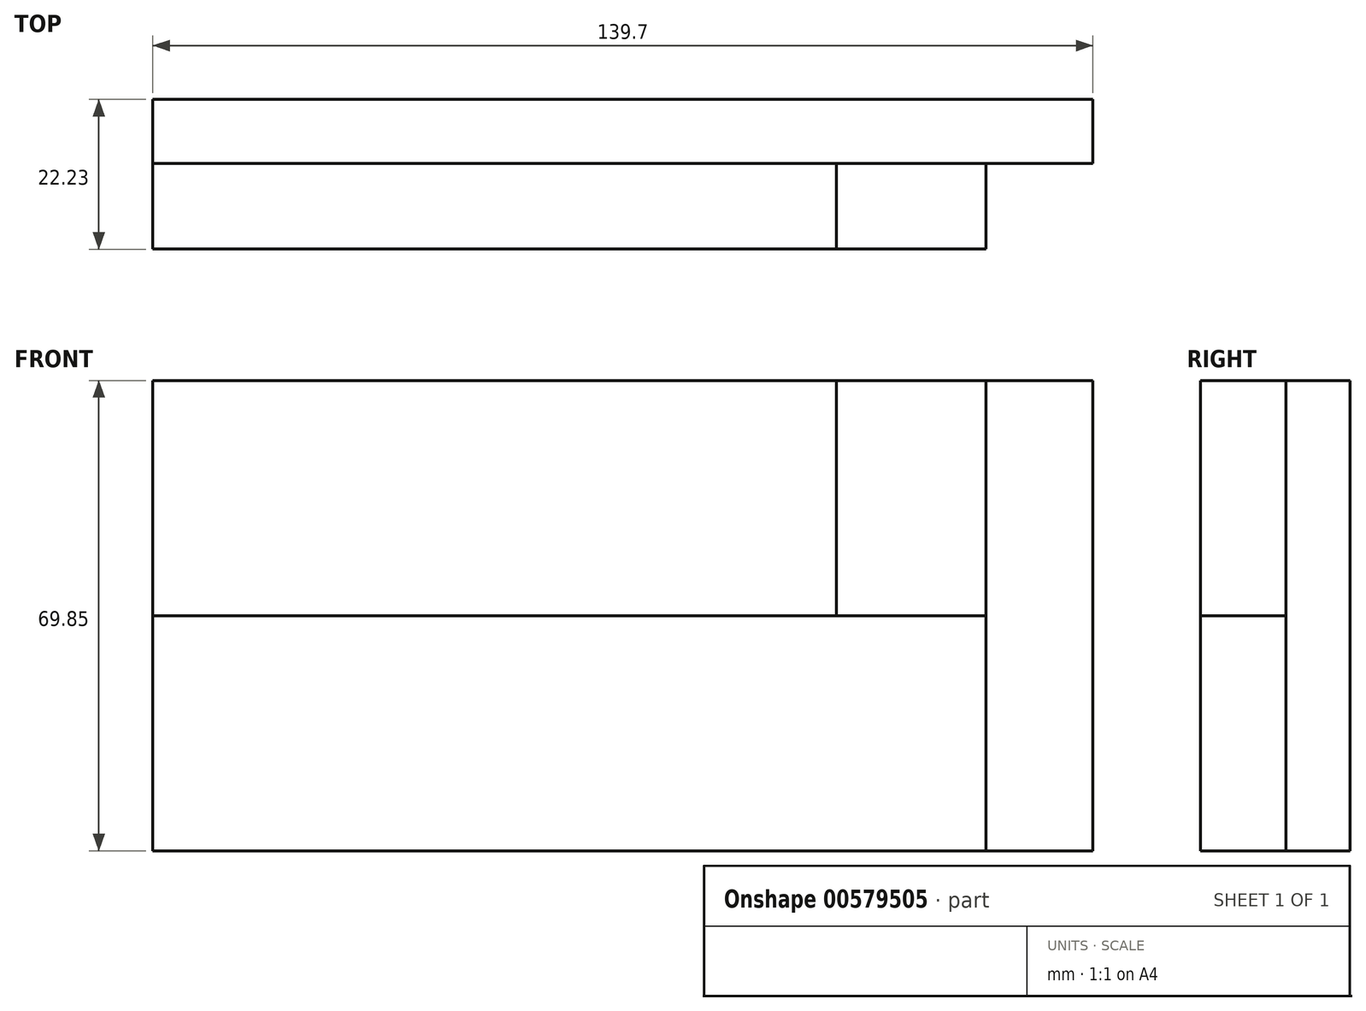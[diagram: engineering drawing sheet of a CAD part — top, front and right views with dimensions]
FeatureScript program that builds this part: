
annotation { "Feature Type Name" : "Feature", "Feature Type Description" : "" }
export const myFeature = defineFeature(function(context is Context, id is Id, definition is map)
    precondition{}
    {
        {
            var Q0;
            Q0=qCreatedBy(makeId("Front.planeOp"),FACE);
            var sketch = newSketch(context, id + "F0", { "sketchPlane" : qUnion([Q0])});
            skLineSegment(sketch, "E0.bottom", {"start": v(-44.43, 29.84) * mm, "end": v(95.27, 29.84) * mm});
            skLineSegment(sketch, "E0.top", {"start": v(-44.43, -40.01) * mm, "end": v(95.27, -40.01) * mm});
            skLineSegment(sketch, "E0.left", {"start": v(-44.43, 29.84) * mm, "end": v(-44.43, -40.01) * mm});
            skLineSegment(sketch, "E0.right", {"start": v(95.27, 29.84) * mm, "end": v(95.27, -40.01) * mm});
            skSolve(sketch);
        }
        {
            var Q0;
            Q0 = qSketchRegion(id + "F0", true);
            extrude(context, id + "F1", {"entities" : qUnion([Q0]), "depth" : 9.52 * mm, "offsetDistance" : 25.4 * mm});
        }
        {
            var Q0;
            Q0=makeQuery(id+"F1.opExtrude","CAP_FACE",FACE,{"disambiguationData":[OSD([sQuery(id+"F0.wireOp",EDGE,"E0.bottom"),sQuery(id+"F0.wireOp",EDGE,"E0.top"),sQuery(id+"F0.wireOp",EDGE,"E0.left"),sQuery(id+"F0.wireOp",EDGE,"E0.right")])],"isStart":false});
            var sketch = newSketch(context, id + "F2", { "sketchPlane" : qUnion([Q0])});
            skLineSegment(sketch, "E1.bottom", {"start": v(-44.43, -5.09) * mm, "end": v(79.4, -5.09) * mm});
            skLineSegment(sketch, "E1.top", {"start": v(-44.43, -40.01) * mm, "end": v(79.4, -40.01) * mm});
            skLineSegment(sketch, "E1.left", {"start": v(-44.43, -5.09) * mm, "end": v(-44.43, -40.01) * mm});
            skLineSegment(sketch, "E1.right", {"start": v(79.4, -5.09) * mm, "end": v(79.4, -40.01) * mm});
            skSolve(sketch);
        }
        {
            var Q0;
            Q0 = qSketchRegion(id + "F2", true);
            extrude(context, id + "F3", {"entities" : qUnion([Q0]), "operationType" : NewBodyOperationType.ADD, "depth" : 12.7 * mm, "offsetDistance" : 25.4 * mm});
        }
        {
            var Q0;
            Q0=makeQuery(id+"F1.opExtrude","CAP_FACE",FACE,{"disambiguationData":[OSD([sQuery(id+"F0.wireOp",EDGE,"E0.bottom"),sQuery(id+"F0.wireOp",EDGE,"E0.top"),sQuery(id+"F0.wireOp",EDGE,"E0.left"),sQuery(id+"F0.wireOp",EDGE,"E0.right")])],"isStart":false});
            var sketch = newSketch(context, id + "F4", { "sketchPlane" : qUnion([Q0])});
            skLineSegment(sketch, "E2.bottom", {"start": v(79.4, -5.09) * mm, "end": v(57.17, -5.09) * mm});
            skLineSegment(sketch, "E2.top", {"start": v(79.4, 29.84) * mm, "end": v(57.17, 29.84) * mm});
            skLineSegment(sketch, "E2.left", {"start": v(79.4, -5.09) * mm, "end": v(79.4, 29.84) * mm});
            skLineSegment(sketch, "E2.right", {"start": v(57.17, -5.09) * mm, "end": v(57.17, 29.84) * mm});
            skSolve(sketch);
        }
        {
            var Q0;
            Q0=makeQuery(id+"F4.imprint","IMPRINT",FACE,{"disambiguationData":[TD([[makeQuery(id+"F4.imprint","IMPRINT",EDGE,{"derivedFrom":sQuery(id+"F4.wireOp",EDGE,"E2.bottom")}),1.0]])]});
            extrude(context, id + "F5", {"entities" : qUnion([Q0]), "depth" : 12.7 * mm, "offsetDistance" : 25.4 * mm});
        }
    });
